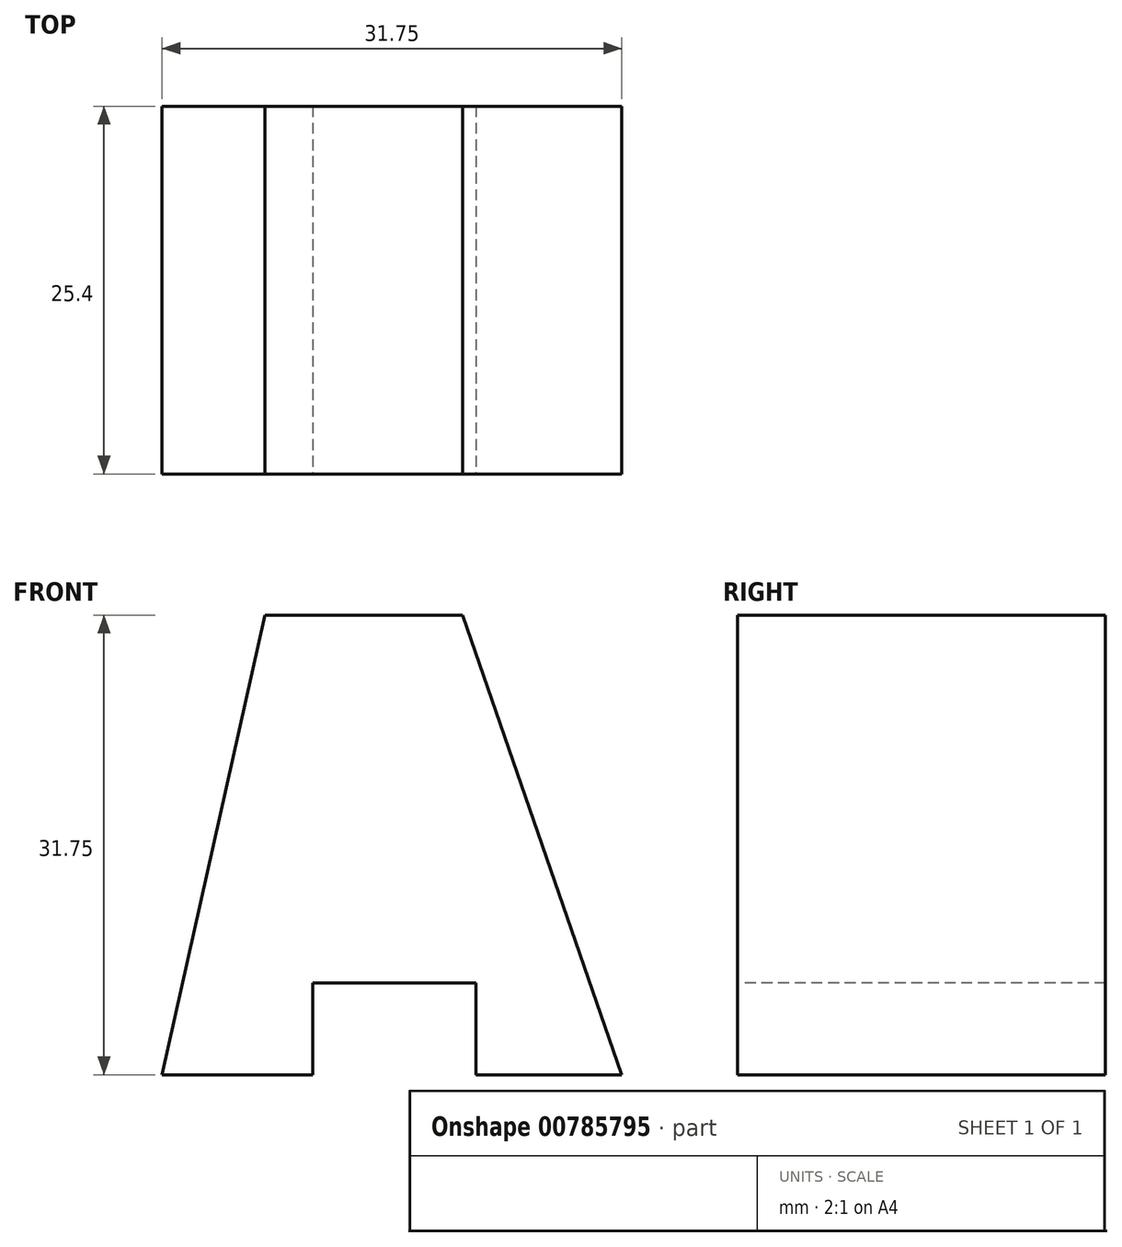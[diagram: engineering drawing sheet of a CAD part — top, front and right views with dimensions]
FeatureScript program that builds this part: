
annotation { "Feature Type Name" : "Feature", "Feature Type Description" : "" }
export const myFeature = defineFeature(function(context is Context, id is Id, definition is map)
    precondition{}
    {
        {
            var Q0;
            Q0=qCreatedBy(makeId("Front.planeOp"),FACE);
            var sketch = newSketch(context, id + "F0", { "sketchPlane" : qUnion([Q0])});
            skLineSegment(sketch, "E0", {"start": v(0, 0) * mm, "end": v(12.7, 0) * mm});
            skLineSegment(sketch, "E1", {"start": v(12.7, 0) * mm, "end": v(12.7, 31.75) * mm});
            skLineSegment(sketch, "E2", {"start": v(12.7, 31.75) * mm, "end": v(-19.05, 31.75) * mm});
            skLineSegment(sketch, "E3", {"start": v(-19.05, 31.75) * mm, "end": v(-19.05, 0) * mm});
            skLineSegment(sketch, "E4", {"start": v(-19.05, 0) * mm, "end": v(0, 0) * mm});
            skSolve(sketch);
        }
        {
            var Q0;
            Q0=makeQuery(id+"F0.imprint","IMPRINT",FACE,{"disambiguationData":[TD([[makeQuery(id+"F0.imprint","IMPRINT",EDGE,{"derivedFrom":sQuery(id+"F0.wireOp",EDGE,"E0")}),1.0]])]});
            extrude(context, id + "F1", {"entities" : qUnion([Q0]), "depth" : 25.4 * mm, "offsetDistance" : 25.4 * mm});
        }
        {
            var Q0;
            Q0=makeQuery(id+"F1.opExtrude","CAP_FACE",FACE,{"disambiguationData":[OSD([sQuery(id+"F0.wireOp",EDGE,"E0"),sQuery(id+"F0.wireOp",EDGE,"E1"),sQuery(id+"F0.wireOp",EDGE,"E2"),sQuery(id+"F0.wireOp",EDGE,"E3"),sQuery(id+"F0.wireOp",EDGE,"E4")])],"isStart":false});
            var sketch = newSketch(context, id + "F2", { "sketchPlane" : qUnion([Q0])});
            skLineSegment(sketch, "E5", {"start": v(12.7, 31.75) * mm, "end": v(1.7, 31.75) * mm});
            skLineSegment(sketch, "E6", {"start": v(12.7, 0) * mm, "end": v(1.7, 31.75) * mm});
            skSolve(sketch);
        }
        {
            var Q0;
            Q0=makeQuery(id+"F2.imprint","IMPRINT",FACE,{"disambiguationData":[TD([[makeQuery(id+"F2.imprint","IMPRINT",EDGE,{"derivedFrom":sQuery(id+"F2.wireOp",EDGE,"E5")}),1.0]])]});
            extrude(context, id + "F3", {"entities" : qUnion([Q0]), "operationType" : NewBodyOperationType.REMOVE, "oppositeDirection" : true, "depth" : 25.4 * mm, "offsetDistance" : 25.4 * mm});
        }
        {
            var Q0;
            Q0=makeQuery(id+"F1.opExtrude","CAP_FACE",FACE,{"disambiguationData":[OSD([sQuery(id+"F0.wireOp",EDGE,"E0"),sQuery(id+"F0.wireOp",EDGE,"E1"),sQuery(id+"F0.wireOp",EDGE,"E2"),sQuery(id+"F0.wireOp",EDGE,"E3"),sQuery(id+"F0.wireOp",EDGE,"E4")])],"isStart":false});
            var sketch = newSketch(context, id + "F4", { "sketchPlane" : qUnion([Q0])});
            skLineSegment(sketch, "E7", {"start": v(-19.05, 31.75) * mm, "end": v(-11.94, 31.75) * mm});
            skLineSegment(sketch, "E8", {"start": v(-19.05, 0) * mm, "end": v(-11.94, 31.75) * mm});
            skSolve(sketch);
        }
        {
            var Q0;
            Q0=makeQuery(id+"F4.imprint","IMPRINT",FACE,{"disambiguationData":[TD([[makeQuery(id+"F4.imprint","IMPRINT",EDGE,{"derivedFrom":sQuery(id+"F4.wireOp",EDGE,"E7")}),1.0]])]});
            extrude(context, id + "F5", {"entities" : qUnion([Q0]), "operationType" : NewBodyOperationType.REMOVE, "oppositeDirection" : true, "depth" : 25.4 * mm, "offsetDistance" : 25.4 * mm});
        }
        {
            var Q0;
            Q0=makeQuery(id+"F1.opExtrude","CAP_FACE",FACE,{"disambiguationData":[OSD([sQuery(id+"F0.wireOp",EDGE,"E0"),sQuery(id+"F0.wireOp",EDGE,"E1"),sQuery(id+"F0.wireOp",EDGE,"E2"),sQuery(id+"F0.wireOp",EDGE,"E3"),sQuery(id+"F0.wireOp",EDGE,"E4")])],"isStart":false});
            var sketch = newSketch(context, id + "F6", { "sketchPlane" : qUnion([Q0])});
            skLineSegment(sketch, "E9", {"start": v(-19.05, 0) * mm, "end": v(-8.64, 0) * mm});
            skLineSegment(sketch, "E10", {"start": v(-8.64, 6.35) * mm, "end": v(-8.64, 0) * mm});
            skLineSegment(sketch, "E11", {"start": v(-8.64, 6.35) * mm, "end": v(2.64, 6.35) * mm});
            skLineSegment(sketch, "E12", {"start": v(2.64, 6.35) * mm, "end": v(2.64, 0) * mm});
            skSolve(sketch);
        }
        {
            var Q0;
            {var subQ0=sQuery(id+"F6.wireOp",EDGE,"E10");Q0=makeQuery(id+"F6.imprint","IMPRINT",FACE,{"disambiguationData":[TD([[makeQuery(id+"F6.imprint","IMPRINT",EDGE,{"derivedFrom":subQ0}),1.0]])]});}
            extrude(context, id + "F7", {"entities" : qUnion([Q0]), "operationType" : NewBodyOperationType.REMOVE, "oppositeDirection" : true, "depth" : 25.4 * mm, "offsetDistance" : 25.4 * mm});
        }
    });
